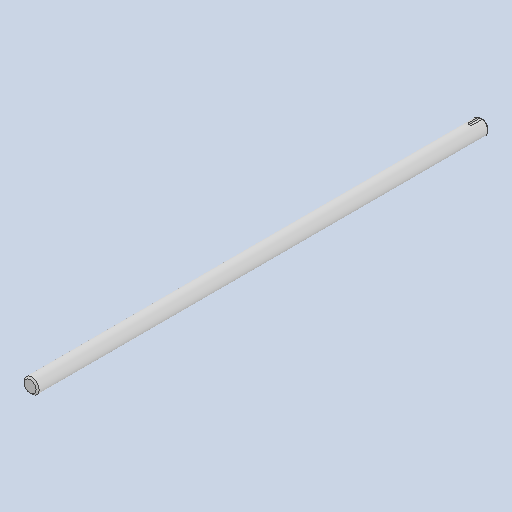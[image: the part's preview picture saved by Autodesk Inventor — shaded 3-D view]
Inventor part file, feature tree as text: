
AUTODESK INVENTOR PART (.ipt)
format: ipt  version: 2025.1 (Build 291241000, 241)  size: 107,008 bytes
history: native  units: in
note: dims shown in document units (in); Inventor stores cm internally (conversion verified against a paired STEP export)
features: other x3, sketch x1, plane x1
ambient origin geometry x8: Origin, YZ Plane, XZ Plane, XY Plane, X Axis, Y Axis, Z Axis, Center Point
bodies: Solid1 (feature_tree)
feature tree (5):
  other  "1886K21_Rotary Shaft (1).ipt"
  other  "Solid1::1886K21_Rotary Shaft (1).ipt"
  other  "TaggingFeature1"
  sketch  "Sketch3"  dims[d0=0.3937in]
  plane  "Work Plane1"
